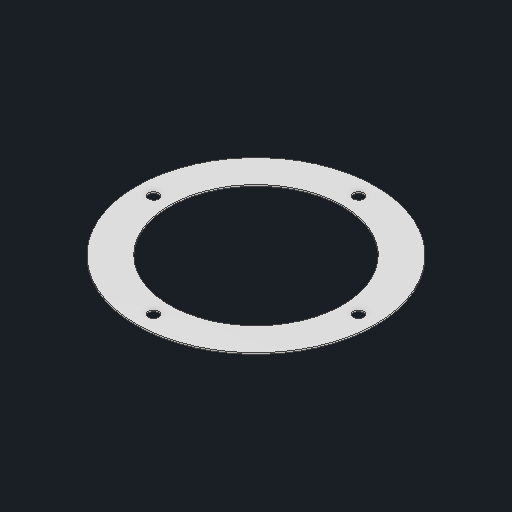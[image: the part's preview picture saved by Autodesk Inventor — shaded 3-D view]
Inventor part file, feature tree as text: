
AUTODESK INVENTOR PART (.ipt)
format: ipt  version: 2025 (Build 290162000, 162)  size: 92,672 bytes
history: native  units: in
note: dims shown in document units (in); Inventor stores cm internally (conversion verified against a paired STEP export)
features: extrude x1
ambient origin geometry x8: Origin, YZ Plane, XZ Plane, XY Plane, X Axis, Y Axis, Z Axis, Center Point
bodies: Solid1 (feature_tree)
feature tree (1):
  extrude  "Extrude1"  [1 undecoded]
note: 1 required parameter value undecoded (feature->parameter linkage not recoverable at this tier; creation-order binding heuristic only, values carry confidence <= 0.55)
